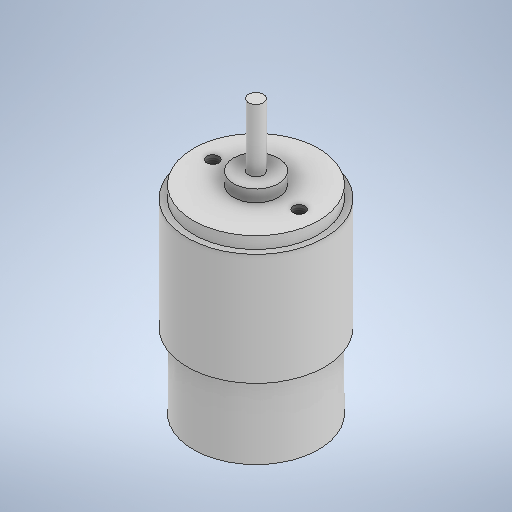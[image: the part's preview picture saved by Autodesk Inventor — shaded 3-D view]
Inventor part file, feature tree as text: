
AUTODESK INVENTOR PART (.ipt)
format: ipt  version: 2025 (Build 290162000, 162)  size: 277,504 bytes
history: native  units: mm
features: extrude x5, sketch x5, other x4
ambient origin geometry x8: Origin, YZ Plane, XZ Plane, XY Plane, X Axis, Y Axis, Z Axis, Center Point
bodies: Body1 (feature_tree)
feature tree (14):
  other  "솔리드1"
  extrude  "돌출1"  Depth=42.0mm
  extrude  "돌출2"  Depth=66.5mm TaperAngle=0.0deg
  extrude  "돌출3"  Depth=15.0mm
  extrude  "돌출4"  Depth=4.0mm TaperAngle=0.0deg
  other  "스레드1"
  other  "스레드2"
  other  "작업 평면1"
  extrude  "돌출5"  Depth=5.0mm
  sketch  "스케치1"
  sketch  "스케치2"
  sketch  "스케치3"
  sketch  "스케치4"
  sketch  "스케치5"
